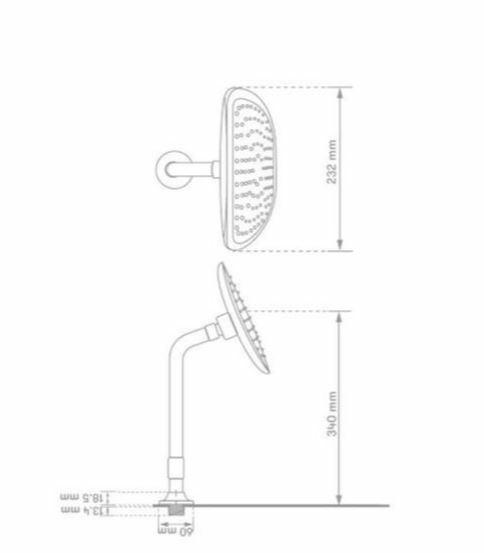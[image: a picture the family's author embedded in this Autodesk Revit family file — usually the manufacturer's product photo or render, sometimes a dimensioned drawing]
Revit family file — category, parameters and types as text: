
# Revit family: 01-2845-11 MEZCLADOR DUCHA 8 SST PRISTINA
name_source: partatom
category: Aparatos sanitarios
revit_build: Autodesk Revit 2018 (Build: 20170223_1515(x64)
units: mm (PartAtom-declared; Revit-internal decimal feet)

## family parameters
Anfitrión = Cara
Compartido = No
Corte con vacíos al cargar = No
Cota de conector redondo = Diámetro de uso
Número OmniClass = 23.31.11.00
Punto de cálculo de habitación = No
Tipo de pieza = Normal

## types (1)
- 01-2845-11
    Alto = 60 mm  [stored 0.19685 ft]
    Ancho = 60 mm  [stored 0.19685 ft]
    Conexión AC = Sí
    Conexión AF = Sí
    Conexión de residuos = No
    Conexión de ventilación = No
    Descripción = Mezclador ducha
    Distancia entre griferias = 203.2 mm  [stored 0.666667 ft]
    Elevación por defecto = 0 mm  [stored 0 ft]
    Fabricante = Gricol
    Imagen de tipo = <Ninguno>
    Link Ficha Tecnica = http://infotecnica.gricol.com
    Metal Acero Inoxidable Cromado = Metal Acero Inoxidable Cromado
    Metal Laton Cromado = Metal Laton Cromado
    Mezclador = Mezclador
    Modelo = 01-2845-11
    Plastico ABS Cromado = Plastico ABS Cromado
    Product Name = MEZCLADOR DUCHA 8 SST PRISTINA
    Profundidad = 210 mm  [stored 0.688976 ft]
    Sepacion entre registro y ducha = 400 mm  [stored 1.31234 ft]
    URL = https://www.gricol.com

note: [stored X ft] marks values corroborated as IEEE doubles in the binary element streams (Revit-internal decimal feet)

## geometry (parser evidence)
native form markers: Blend x2, Sweep x26
no freeform markers — native parametric forms only
